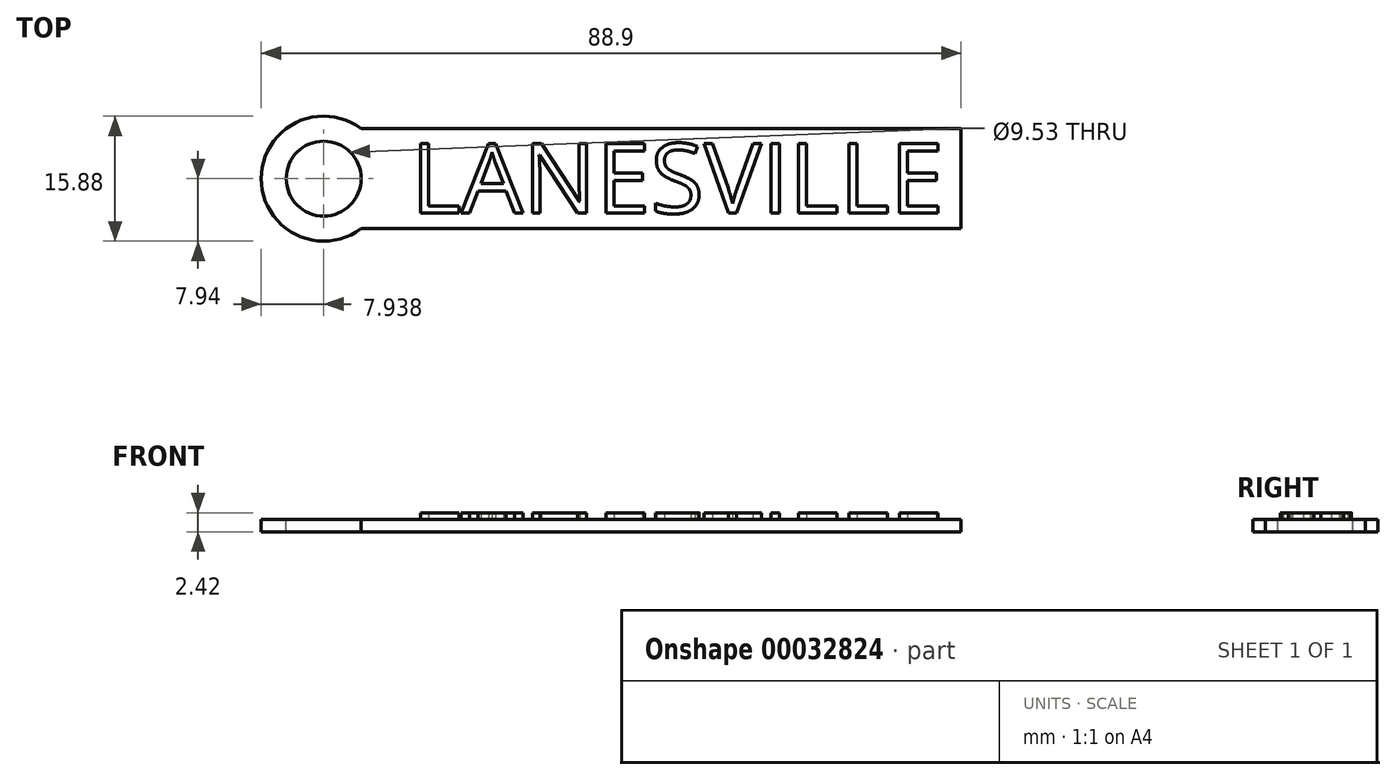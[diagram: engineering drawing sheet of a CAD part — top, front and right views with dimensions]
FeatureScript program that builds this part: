
annotation { "Feature Type Name" : "Feature", "Feature Type Description" : "" }
export const myFeature = defineFeature(function(context is Context, id is Id, definition is map)
    precondition{}
    {
        {
            var Q0;
            Q0=qCreatedBy(makeId("Top.planeOp"),FACE);
            var sketch = newSketch(context, id + "F0", { "sketchPlane" : qUnion([Q0])});
            skLineSegment(sketch, "E0.rect.bottom", {"start": v(38.1, 6.35) * mm, "end": v(-38.1, 6.35) * mm});
            skLineSegment(sketch, "E0.rect.top", {"start": v(38.1, -6.35) * mm, "end": v(-38.1, -6.35) * mm});
            skLineSegment(sketch, "E0.rect.left", {"start": v(38.1, 6.35) * mm, "end": v(38.1, -6.35) * mm});
            skLineSegment(sketch, "E0.rect.right", {"start": v(-38.1, 6.35) * mm, "end": v(-38.1, -6.35) * mm});
            skPoint(sketch, "E0.rect.middle", {"position": v(0, 0) * mm});
            skSolve(sketch);
        }
        {
            var Q0;
            Q0 = qSketchRegion(id + "F0", true);
            extrude(context, id + "F1", {"entities" : qUnion([Q0]), "oppositeDirection" : true, "depth" : 1.59 * mm});
        }
        {
            var Q0;
            Q0=makeQuery(id+"F1.opExtrude","CAP_FACE",FACE,{"disambiguationData":[OSD([sQuery(id+"F0.wireOp",EDGE,"E0.rect.bottom"),sQuery(id+"F0.wireOp",EDGE,"E0.rect.top"),sQuery(id+"F0.wireOp",EDGE,"E0.rect.left"),sQuery(id+"F0.wireOp",EDGE,"E0.rect.right")])],"isStart":true});
            var sketch = newSketch(context, id + "F2", { "sketchPlane" : qUnion([Q0])});
            skText(sketch, "E1", { "text": "LANESVILLE\n", "fontName": "OpenSans-Regular.ttf"});
            skLineSegment(sketch, "E2", {"start": v(-31.8, -4.38) * mm, "end": v(35.12, 4.5) * mm, "construction": true});
            const initialGuessF2  = {"E1": [-0.0318, -0.00438, 1, 0, 0.0089]};
            skSetInitialGuess(sketch, initialGuessF2);
            skSolve(sketch);
        }
        {
            var Q0;
            Q0 = qSketchRegion(id + "F2", true);
            extrude(context, id + "F3", {"entities" : qUnion([Q0]), "operationType" : NewBodyOperationType.ADD, "depth" : 0.83 * mm});
        }
        {
            var Q0;
            {var subQ0=sQuery(id+"F0.wireOp",EDGE,"E0.rect.bottom");var subQ1=sQuery(id+"F0.wireOp",EDGE,"E0.rect.top");var subQ2=sQuery(id+"F0.wireOp",EDGE,"E0.rect.left");var subQ3=sQuery(id+"F0.wireOp",EDGE,"E0.rect.right");Q0=makeQuery(id+"F3.boolean.opBoolean","SPLIT",FACE,{"disambiguationData":[TD([makeQuery(id+"F1.opExtrude","SWEPT_FACE",FACE,{"disambiguationData":[OSD([subQ0])]})])],"derivedFrom":makeQuery(id+"F1.opExtrude","CAP_FACE",FACE,{"disambiguationData":[OSD([subQ0,subQ1,subQ2,subQ3])],"isStart":true})});}
            var sketch = newSketch(context, id + "F4", { "sketchPlane" : qUnion([Q0])});
            skCircle(sketch, "E3", {"center": v(-42.86, 0) * mm, "radius": 7.94 * mm});
            skCircle(sketch, "E4", {"center": v(-42.86, 0) * mm, "radius": 4.76 * mm});
            skSolve(sketch);
        }
        {
            var Q0;
            Q0 = qSketchRegion(id + "F4", true);
            var Q1;
            Q1=makeQuery(id+"F1.opExtrude","CAP_FACE",FACE,{"disambiguationData":[OSD([sQuery(id+"F0.wireOp",EDGE,"E0.rect.bottom"),sQuery(id+"F0.wireOp",EDGE,"E0.rect.top"),sQuery(id+"F0.wireOp",EDGE,"E0.rect.left"),sQuery(id+"F0.wireOp",EDGE,"E0.rect.right")])],"isStart":false});
            extrude(context, id + "F5", {"entities" : qUnion([Q0]), "operationType" : NewBodyOperationType.ADD, "endBound" : BoundingType.UP_TO_SURFACE, "oppositeDirection" : true, "endBoundEntityFace" : qUnion([Q1]), "depth" : 25.4 * mm});
        }
    });
